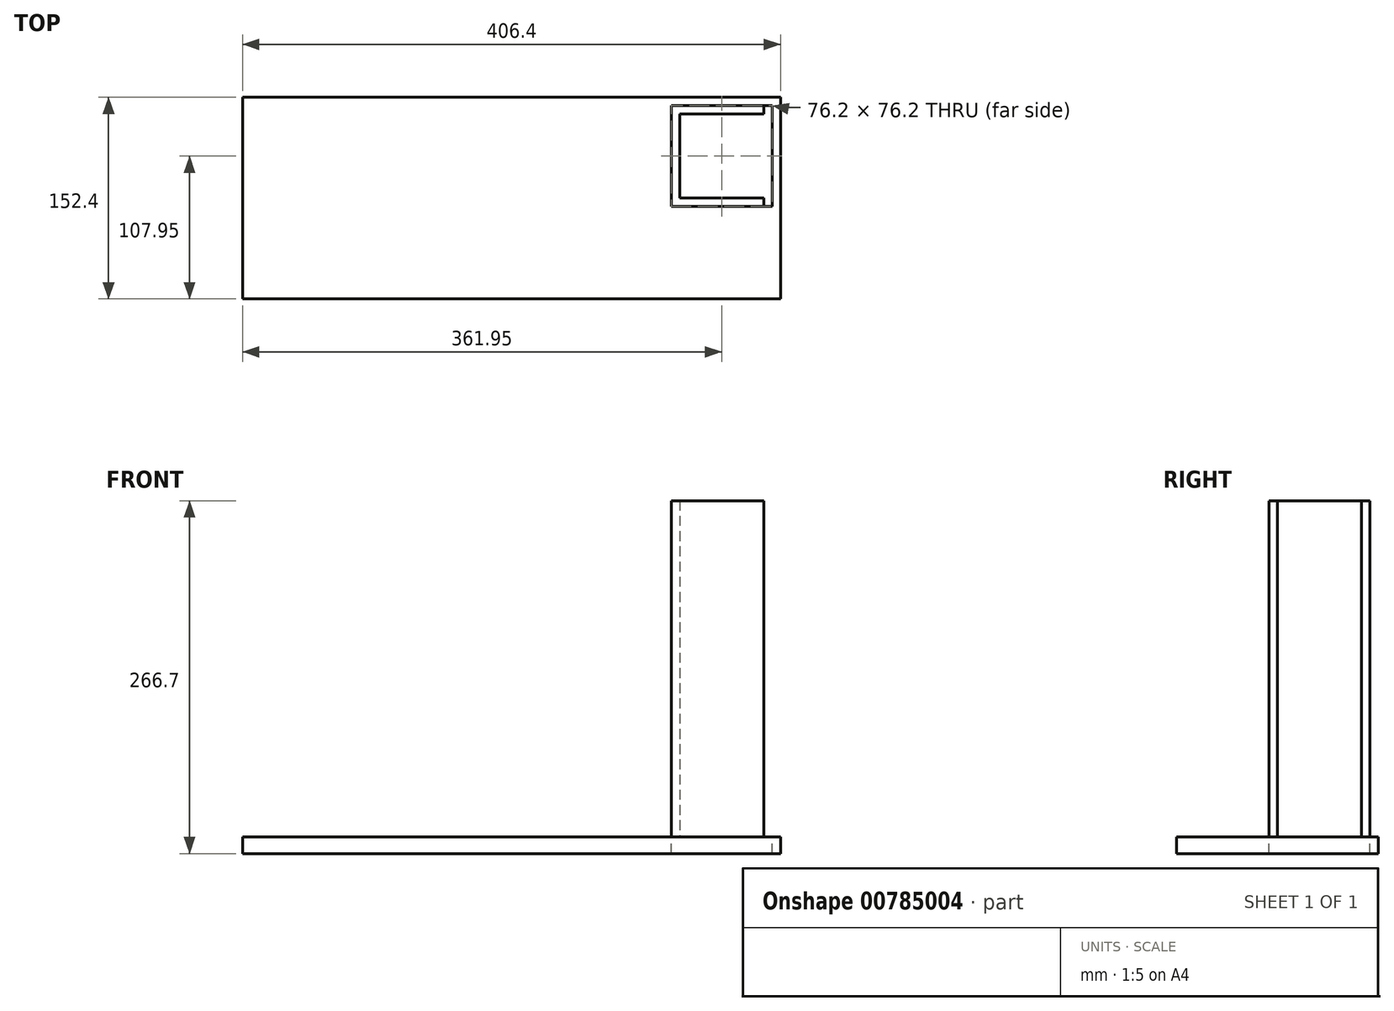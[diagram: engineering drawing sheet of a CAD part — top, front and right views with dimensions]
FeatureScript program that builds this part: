
annotation { "Feature Type Name" : "Feature", "Feature Type Description" : "" }
export const myFeature = defineFeature(function(context is Context, id is Id, definition is map)
    precondition{}
    {
        {
            var Q0;
            Q0=qCreatedBy(makeId("Top.planeOp"),FACE);
            var sketch = newSketch(context, id + "F0", { "sketchPlane" : qUnion([Q0])});
            skLineSegment(sketch, "E0.bottom", {"start": v(203.2, -76.2) * mm, "end": v(-203.2, -76.2) * mm});
            skLineSegment(sketch, "E0.top", {"start": v(203.2, 76.2) * mm, "end": v(-203.2, 76.2) * mm});
            skLineSegment(sketch, "E0.left", {"start": v(203.2, -76.2) * mm, "end": v(203.2, 76.2) * mm});
            skLineSegment(sketch, "E0.right", {"start": v(-203.2, -76.2) * mm, "end": v(-203.2, 76.2) * mm});
            skPoint(sketch, "E0.middle", {"position": v(0, 0) * mm});
            skLineSegment(sketch, "E1.bottom", {"start": v(190.5, 0) * mm, "end": v(127, 0) * mm});
            skLineSegment(sketch, "E1.top", {"start": v(190.5, 63.5) * mm, "end": v(127, 63.5) * mm});
            skLineSegment(sketch, "E1.left", {"start": v(190.5, 0) * mm, "end": v(190.5, 63.5) * mm});
            skLineSegment(sketch, "E1.right", {"start": v(127, 0) * mm, "end": v(127, 63.5) * mm});
            skLineSegment(sketch, "E2.bottom", {"start": v(120.65, 69.85) * mm, "end": v(196.85, 69.85) * mm});
            skLineSegment(sketch, "E2.top", {"start": v(120.65, -6.35) * mm, "end": v(196.85, -6.35) * mm});
            skLineSegment(sketch, "E2.left", {"start": v(120.65, 69.85) * mm, "end": v(120.65, -6.35) * mm});
            skLineSegment(sketch, "E2.right", {"start": v(196.85, 69.85) * mm, "end": v(196.85, -6.35) * mm});
            skLineSegment(sketch, "E3", {"start": v(190.5, 63.5) * mm, "end": v(190.5, 69.85) * mm});
            skLineSegment(sketch, "E4", {"start": v(190.5, 0) * mm, "end": v(190.5, -6.35) * mm});
            skSolve(sketch);
        }
        {
            var Q0;
            Q0=makeQuery(id+"F0.imprint","IMPRINT",FACE,{"disambiguationData":[TD([[makeQuery(id+"F0.imprint","IMPRINT",EDGE,{"derivedFrom":sQuery(id+"F0.wireOp",EDGE,"E0.bottom")}),-1.0]])]});
            extrude(context, id + "F1", {"entities" : qUnion([Q0]), "oppositeDirection" : true, "depth" : 12.7 * mm, "offsetDistance" : 25.4 * mm});
        }
        {
            var Q0;
            Q0=makeQuery(id+"F0.imprint","IMPRINT",FACE,{"disambiguationData":[TD([[makeQuery(id+"F0.imprint","IMPRINT",EDGE,{"derivedFrom":sQuery(id+"F0.wireOp",EDGE,"E1.bottom")}),1.0]])]});
            extrude(context, id + "F2", {"entities" : qUnion([Q0]), "depth" : 254 * mm, "offsetDistance" : 25.4 * mm});
        }
    });
